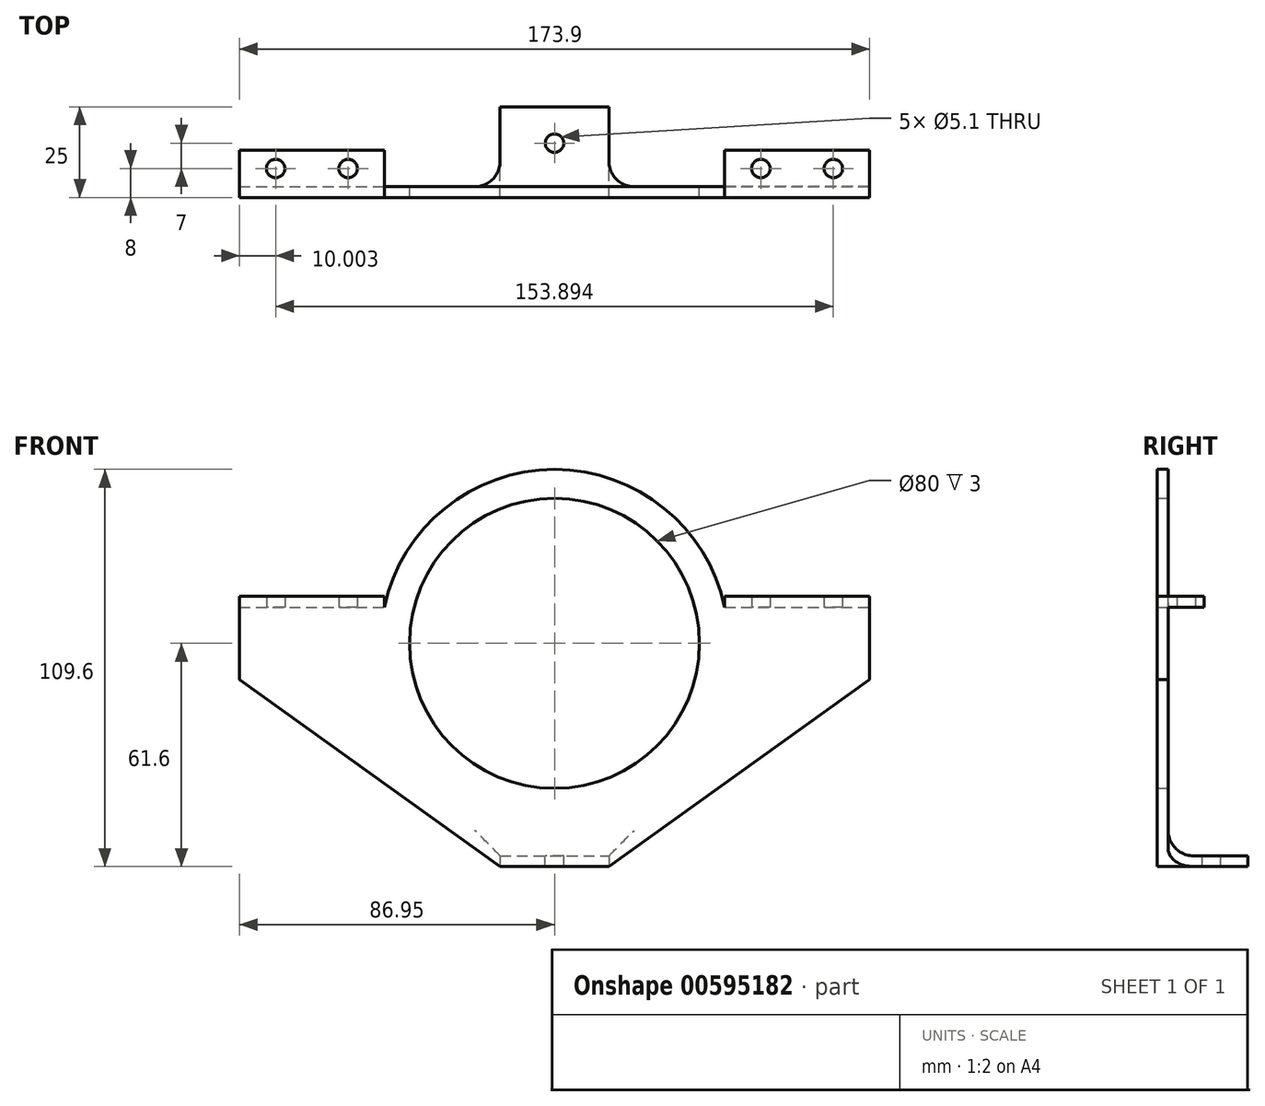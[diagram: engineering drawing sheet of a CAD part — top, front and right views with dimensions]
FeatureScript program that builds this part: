
annotation { "Feature Type Name" : "Feature", "Feature Type Description" : "" }
export const myFeature = defineFeature(function(context is Context, id is Id, definition is map)
    precondition{}
    {
        {
            var Q0;
            Q0=qCreatedBy(makeId("Front.planeOp"),FACE);
            var sketch = newSketch(context, id + "F0", { "sketchPlane" : qUnion([Q0])});
            skCircle(sketch, "E0", {"center": v(0, 0) * mm, "radius": 40 * mm});
            skCircle(sketch, "E1", {"center": v(0, 0) * mm, "radius": 48 * mm});
            skLineSegment(sketch, "E2.bottom", {"start": v(-86.95, 10) * mm, "end": v(-38.73, 10) * mm});
            skLineSegment(sketch, "E2.top", {"start": v(-86.95, -10) * mm, "end": v(-38.73, -10) * mm});
            skLineSegment(sketch, "E2.left", {"start": v(-86.95, 10) * mm, "end": v(-86.95, -10) * mm});
            skLineSegment(sketch, "E2.right", {"start": v(-38.73, 10) * mm, "end": v(-38.73, -10) * mm});
            skLineSegment(sketch, "E3.bottom", {"start": v(38.73, 10) * mm, "end": v(86.95, 10) * mm});
            skLineSegment(sketch, "E3.top", {"start": v(38.73, -10) * mm, "end": v(86.95, -10) * mm});
            skLineSegment(sketch, "E3.left", {"start": v(38.73, 10) * mm, "end": v(38.73, -10) * mm});
            skLineSegment(sketch, "E3.right", {"start": v(86.95, 10) * mm, "end": v(86.95, -10) * mm});
            skPoint(sketch, "E4", {"position": v(-46.95, 10) * mm});
            skPoint(sketch, "E5", {"position": v(46.95, 10) * mm});
            skLineSegment(sketch, "E6.bottom", {"start": v(-15, -37.08) * mm, "end": v(15, -37.08) * mm});
            skLineSegment(sketch, "E6.top", {"start": v(-15, -58.6) * mm, "end": v(15, -58.6) * mm});
            skLineSegment(sketch, "E6.left", {"start": v(-15, -37.08) * mm, "end": v(-15, -58.6) * mm});
            skLineSegment(sketch, "E6.right", {"start": v(15, -37.08) * mm, "end": v(15, -58.6) * mm});
            skPoint(sketch, "E7", {"position": v(15, -45.6) * mm});
            skLineSegment(sketch, "E8", {"start": v(-86.95, -10) * mm, "end": v(-15, -61.6) * mm});
            skLineSegment(sketch, "E9.top", {"start": v(-15, -61.6) * mm, "end": v(15, -61.6) * mm});
            skLineSegment(sketch, "E9.left", {"start": v(-15, -58.6) * mm, "end": v(-15, -61.6) * mm});
            skLineSegment(sketch, "E9.right", {"start": v(15, -58.6) * mm, "end": v(15, -61.6) * mm});
            skLineSegment(sketch, "E10", {"start": v(86.95, -10) * mm, "end": v(15, -61.6) * mm});
            skSolve(sketch);
        }
        {
            var Q0;
            {var subQ5=sQuery(id+"F0.wireOp",EDGE,"E2.left");Q0=makeQuery(id+"F0.imprint","IMPRINT",FACE,{"disambiguationData":[TD([[makeQuery(id+"F0.imprint","IMPRINT",EDGE,{"derivedFrom":subQ5}),1.0]])]});}
            var Q1;
            {var subQ5=sQuery(id+"F0.wireOp",EDGE,"E3.right");Q1=makeQuery(id+"F0.imprint","IMPRINT",FACE,{"disambiguationData":[TD([[makeQuery(id+"F0.imprint","IMPRINT",EDGE,{"derivedFrom":subQ5}),-1.0]])]});}
            var Q2;
            {var subQ5=sQuery(id+"F0.wireOp",EDGE,"E6.top");Q2=makeQuery(id+"F0.imprint","IMPRINT",FACE,{"disambiguationData":[TD([[makeQuery(id+"F0.imprint","IMPRINT",EDGE,{"derivedFrom":subQ5}),1.0]])]});}
            var Q3;
            {var subQ0=sQuery(id+"F0.wireOp",EDGE,"E2.bottom");var subQ5=sQuery(id+"F0.wireOp",EDGE,"E1");var subQ6=makeQuery(id+"F0.imprint","INTERSECT",VERTEX,{"derivedFrom":[subQ5,subQ0]});Q3=makeQuery(id+"F0.imprint","IMPRINT",FACE,{"disambiguationData":[TD([[makeQuery(id+"F0.imprint","IMPRINT",EDGE,{"disambiguationData":[TD([[subQ6,1.0]])],"derivedFrom":subQ5}),1.0]])]});}
            var Q4;
            {var subQ0=sQuery(id+"F0.wireOp",EDGE,"E2.top");var subQ5=sQuery(id+"F0.wireOp",EDGE,"E1");var subQ6=makeQuery(id+"F0.imprint","INTERSECT",VERTEX,{"derivedFrom":[subQ5,subQ0]});Q4=makeQuery(id+"F0.imprint","IMPRINT",FACE,{"disambiguationData":[TD([[makeQuery(id+"F0.imprint","IMPRINT",EDGE,{"disambiguationData":[TD([[subQ6,-1.0]])],"derivedFrom":subQ5}),1.0]])]});}
            var Q5;
            {var subQ3=sQuery(id+"F0.wireOp",EDGE,"E6.right");var subQ5=sQuery(id+"F0.wireOp",EDGE,"E1");var subQ6=makeQuery(id+"F0.imprint","INTERSECT",VERTEX,{"derivedFrom":[subQ5,subQ3]});Q5=makeQuery(id+"F0.imprint","IMPRINT",FACE,{"disambiguationData":[TD([[makeQuery(id+"F0.imprint","IMPRINT",EDGE,{"disambiguationData":[TD([[subQ6,-1.0]])],"derivedFrom":subQ5}),1.0]])]});}
            var Q6;
            {var subQ1=sQuery(id+"F0.wireOp",EDGE,"E2.bottom");var subQ6=sQuery(id+"F0.wireOp",EDGE,"E1");var subQ7=makeQuery(id+"F0.imprint","INTERSECT",VERTEX,{"derivedFrom":[subQ6,subQ1]});Q6=makeQuery(id+"F0.imprint","IMPRINT",FACE,{"disambiguationData":[TD([[makeQuery(id+"F0.imprint","IMPRINT",EDGE,{"disambiguationData":[TD([[subQ7,-1.0]])],"derivedFrom":subQ6}),1.0]])]});}
            var Q7;
            {var subQ0=sQuery(id+"F0.wireOp",EDGE,"E6.left");var subQ6=sQuery(id+"F0.wireOp",EDGE,"E1");var subQ7=makeQuery(id+"F0.imprint","INTERSECT",VERTEX,{"derivedFrom":[subQ6,subQ0]});Q7=makeQuery(id+"F0.imprint","IMPRINT",FACE,{"disambiguationData":[TD([[makeQuery(id+"F0.imprint","IMPRINT",EDGE,{"disambiguationData":[TD([[subQ7,-1.0]])],"derivedFrom":subQ6}),1.0]])]});}
            var Q8;
            {var subQ1=sQuery(id+"F0.wireOp",EDGE,"E3.bottom");var subQ6=sQuery(id+"F0.wireOp",EDGE,"E1");var subQ8=makeQuery(id+"F0.imprint","INTERSECT",VERTEX,{"derivedFrom":[subQ6,subQ1]});Q8=makeQuery(id+"F0.imprint","IMPRINT",FACE,{"disambiguationData":[TD([[makeQuery(id+"F0.imprint","IMPRINT",EDGE,{"disambiguationData":[TD([[subQ8,1.0]])],"derivedFrom":subQ6}),1.0]])]});}
            var Q9;
            {var subQ0=sQuery(id+"F0.wireOp",EDGE,"yV94HF0Q-9D82-jIKN-eZ8h-sUfrhPP9Iwmu.left");Q9=makeQuery(id+"F0.imprint","IMPRINT",FACE,{"disambiguationData":[TD([[makeQuery(id+"F0.imprint","IMPRINT",EDGE,{"derivedFrom":subQ0}),-1.0]])]});}
            var Q10;
            {var subQ0=sQuery(id+"F0.wireOp",EDGE,"yV94HF0Q-9D82-jIKN-eZ8h-sUfrhPP9Iwmu.right");Q10=makeQuery(id+"F0.imprint","IMPRINT",FACE,{"disambiguationData":[TD([[makeQuery(id+"F0.imprint","IMPRINT",EDGE,{"derivedFrom":subQ0}),1.0]])]});}
            var Q11;
            Q11=makeQuery(id+"F0.imprint","IMPRINT",FACE,{"disambiguationData":[TD([[makeQuery(id+"F0.imprint","IMPRINT",EDGE,{"derivedFrom":sQuery(id+"F0.wireOp",EDGE,"E6.top")}),-1.0]])]});
            var Q12;
            {var subQ4=sQuery(id+"F0.wireOp",EDGE,"E8");Q12=makeQuery(id+"F0.imprint","IMPRINT",FACE,{"disambiguationData":[TD([[makeQuery(id+"F0.imprint","IMPRINT",EDGE,{"derivedFrom":subQ4}),1.0]])]});}
            var Q13;
            {var subQ0=sQuery(id+"F0.wireOp",EDGE,"E9.right");Q13=makeQuery(id+"F0.imprint","IMPRINT",FACE,{"disambiguationData":[TD([[makeQuery(id+"F0.imprint","IMPRINT",EDGE,{"derivedFrom":subQ0}),1.0]])]});}
            var Q14;
            {var subQ5=sQuery(id+"F0.wireOp",EDGE,"E6.top");Q14=makeQuery(id+"F0.imprint","IMPRINT",FACE,{"disambiguationData":[TD([[makeQuery(id+"F0.imprint","IMPRINT",EDGE,{"derivedFrom":subQ5}),1.0]])]});}
            var Q15;
            Q15=makeQuery(id+"F0.imprint","IMPRINT",FACE,{"disambiguationData":[TD([[makeQuery(id+"F0.imprint","IMPRINT",EDGE,{"derivedFrom":sQuery(id+"F0.wireOp",EDGE,"E6.top")}),-1.0]])]});
            extrude(context, id + "F1", {"entities" : qUnion([Q0, Q1, Q2, Q3, Q4, Q5, Q6, Q7, Q8, Q9, Q10, Q11, Q12, Q13, Q14, Q15]), "depth" : 3 * mm, "offsetDistance" : 25 * mm});
        }
        {
            var Q0;
            Q0=makeQuery(id+"F1.opExtrude","SWEPT_FACE",FACE,{"disambiguationData":[OSD([sQuery(id+"F0.wireOp",EDGE,"E2.bottom")])]});
            var sketch = newSketch(context, id + "F2", { "sketchPlane" : qUnion([Q0])});
            skLineSegment(sketch, "E11.bottom", {"start": v(-86.95, -3) * mm, "end": v(-46.95, -3) * mm});
            skLineSegment(sketch, "E11.top", {"start": v(-86.95, 10) * mm, "end": v(-46.95, 10) * mm});
            skLineSegment(sketch, "E11.left", {"start": v(-86.95, -3) * mm, "end": v(-86.95, 10) * mm});
            skLineSegment(sketch, "E11.right", {"start": v(-46.95, -3) * mm, "end": v(-46.95, 10) * mm});
            skLineSegment(sketch, "E12.bottom", {"start": v(86.95, -3) * mm, "end": v(46.95, -3) * mm});
            skLineSegment(sketch, "E12.top", {"start": v(86.95, 10) * mm, "end": v(46.95, 10) * mm});
            skLineSegment(sketch, "E12.left", {"start": v(86.95, -3) * mm, "end": v(86.95, 10) * mm});
            skLineSegment(sketch, "E12.right", {"start": v(46.95, -3) * mm, "end": v(46.95, 10) * mm});
            skCircle(sketch, "E13", {"center": v(-56.95, 5) * mm, "radius": 2.55 * mm});
            skCircle(sketch, "E14", {"center": v(-76.95, 5) * mm, "radius": 2.55 * mm});
            skCircle(sketch, "E15", {"center": v(56.95, 5) * mm, "radius": 2.55 * mm});
            skCircle(sketch, "E16", {"center": v(76.95, 5) * mm, "radius": 2.55 * mm});
            skSolve(sketch);
        }
        {
            var Q0;
            Q0 = qSketchRegion(id + "F2", true);
            extrude(context, id + "F3", {"entities" : qUnion([Q0]), "operationType" : NewBodyOperationType.ADD, "depth" : 3 * mm, "offsetDistance" : 25 * mm});
        }
        {
            var Q0;
            Q0=makeQuery(id+"F3.boolean.opBoolean","MERGE",FACE,{"derivedFrom":[makeQuery(id+"F1.opExtrude","CAP_FACE",FACE,{"disambiguationData":[OSD([sQuery(id+"F0.wireOp",EDGE,"E0"),sQuery(id+"F0.wireOp",EDGE,"E1"),sQuery(id+"F0.wireOp",EDGE,"E2.bottom"),sQuery(id+"F0.wireOp",EDGE,"E2.top"),sQuery(id+"F0.wireOp",EDGE,"E2.left"),sQuery(id+"F0.wireOp",EDGE,"E3.bottom"),sQuery(id+"F0.wireOp",EDGE,"E3.top"),sQuery(id+"F0.wireOp",EDGE,"E3.right"),sQuery(id+"F0.wireOp",EDGE,"E6.left"),sQuery(id+"F0.wireOp",EDGE,"E6.right"),sQuery(id+"F0.wireOp",EDGE,"E6.top")])],"isStart":false}),makeQuery(id+"F3.opExtrude","SWEPT_FACE",FACE,{"disambiguationData":[OSD([sQuery(id+"F2.wireOp",EDGE,"E11.bottom")])]}),makeQuery(id+"F3.opExtrude","SWEPT_FACE",FACE,{"disambiguationData":[OSD([sQuery(id+"F2.wireOp",EDGE,"E12.bottom")])]})]});
            var sketch = newSketch(context, id + "F4", { "sketchPlane" : qUnion([Q0])});
            skLineSegment(sketch, "E17.bottom", {"start": v(-15, -58.6) * mm, "end": v(15, -58.6) * mm});
            skLineSegment(sketch, "E17.top", {"start": v(-15, -61.6) * mm, "end": v(15, -61.6) * mm});
            skLineSegment(sketch, "E17.left", {"start": v(-15, -58.6) * mm, "end": v(-15, -61.6) * mm});
            skLineSegment(sketch, "E17.right", {"start": v(15, -58.6) * mm, "end": v(15, -61.6) * mm});
            skSolve(sketch);
        }
        {
            var Q0;
            Q0 = qSketchRegion(id + "F4", true);
            extrude(context, id + "F5", {"entities" : qUnion([Q0]), "operationType" : NewBodyOperationType.ADD, "oppositeDirection" : true, "depth" : 25 * mm, "offsetDistance" : 25 * mm});
        }
        {
            var Q0;
            Q0=makeQuery(id+"F5.opExtrude","SWEPT_FACE",FACE,{"disambiguationData":[OSD([sQuery(id+"F4.wireOp",EDGE,"E17.bottom")])]});
            var sketch = newSketch(context, id + "F6", { "sketchPlane" : qUnion([Q0])});
            skCircle(sketch, "E18", {"center": v(0, 12) * mm, "radius": 2.55 * mm});
            skSolve(sketch);
        }
        {
            var Q0;
            Q0 = qSketchRegion(id + "F6", true);
            extrude(context, id + "F7", {"entities" : qUnion([Q0]), "operationType" : NewBodyOperationType.REMOVE, "endBound" : BoundingType.UP_TO_NEXT, "oppositeDirection" : true, "depth" : 25 * mm, "offsetDistance" : 25 * mm});
        }
        {
            var Q0;
            Q0=makeQuery(id+"F5.boolean.opBoolean","INTERSECT",EDGE,{"derivedFrom":[makeQuery(id+"F1.opExtrude","CAP_FACE",FACE,{"disambiguationData":[OSD([sQuery(id+"F0.wireOp",EDGE,"E0"),sQuery(id+"F0.wireOp",EDGE,"E1"),sQuery(id+"F0.wireOp",EDGE,"E2.bottom"),sQuery(id+"F0.wireOp",EDGE,"E2.left"),sQuery(id+"F0.wireOp",EDGE,"E3.bottom"),sQuery(id+"F0.wireOp",EDGE,"E3.right"),sQuery(id+"F0.wireOp",EDGE,"E8"),sQuery(id+"F0.wireOp",EDGE,"E9.top"),sQuery(id+"F0.wireOp",EDGE,"E10")])],"isStart":true}),makeQuery(id+"F5.opExtrude","SWEPT_FACE",FACE,{"disambiguationData":[OSD([sQuery(id+"F4.wireOp",EDGE,"E17.bottom")])]})]});
            var Q1;
            Q1=makeQuery(id+"F5.boolean.opBoolean","INTERSECT",EDGE,{"derivedFrom":[makeQuery(id+"F1.opExtrude","CAP_FACE",FACE,{"disambiguationData":[OSD([sQuery(id+"F0.wireOp",EDGE,"E0"),sQuery(id+"F0.wireOp",EDGE,"E1"),sQuery(id+"F0.wireOp",EDGE,"E2.bottom"),sQuery(id+"F0.wireOp",EDGE,"E2.left"),sQuery(id+"F0.wireOp",EDGE,"E3.bottom"),sQuery(id+"F0.wireOp",EDGE,"E3.right"),sQuery(id+"F0.wireOp",EDGE,"E8"),sQuery(id+"F0.wireOp",EDGE,"E9.top"),sQuery(id+"F0.wireOp",EDGE,"E10")])],"isStart":true}),makeQuery(id+"F5.opExtrude","SWEPT_FACE",FACE,{"disambiguationData":[OSD([sQuery(id+"F4.wireOp",EDGE,"E17.left")])]})]});
            var Q2;
            Q2=makeQuery(id+"F5.boolean.opBoolean","INTERSECT",EDGE,{"derivedFrom":[makeQuery(id+"F1.opExtrude","CAP_FACE",FACE,{"disambiguationData":[OSD([sQuery(id+"F0.wireOp",EDGE,"E0"),sQuery(id+"F0.wireOp",EDGE,"E1"),sQuery(id+"F0.wireOp",EDGE,"E2.bottom"),sQuery(id+"F0.wireOp",EDGE,"E2.left"),sQuery(id+"F0.wireOp",EDGE,"E3.bottom"),sQuery(id+"F0.wireOp",EDGE,"E3.right"),sQuery(id+"F0.wireOp",EDGE,"E8"),sQuery(id+"F0.wireOp",EDGE,"E9.top"),sQuery(id+"F0.wireOp",EDGE,"E10")])],"isStart":true}),makeQuery(id+"F5.opExtrude","SWEPT_FACE",FACE,{"disambiguationData":[OSD([sQuery(id+"F4.wireOp",EDGE,"E17.right")])]})]});
            fillet(context, id + "F8", {"entities" : qUnion([Q0, Q1, Q2]), "radius" : 7 * mm, "tangentPropagation" : true, "allowEdgeOverflow" : false});
        }
    });
